# Revit family: QF_EVEREST_ES_3_cat
name_source: partatom
category: Specialty Equipment
revit_build: Autodesk Revit 2015 (Build: 20160512_0715(x64)
units: mm (PartAtom-declared; Revit-internal decimal feet)

## types (2) — shared parameters
Apparent Power = 0 VA
Conn Conduit = Yes
Cycle = 60 Hz
Depth = 803 mm
Foodservice Equipment Identifier = Yes
Height = 2010 mm  [stored 6.59449 ft]
Identify Quantity as Lot = Yes
Length = 1900 mm  [stored 6.2336 ft]
Manufacturer = EVEREST
Max Overcurrent Protection = 0 A
Min Ckt Ampacity = 0 A
Number of Poles = 1
Phase = 1
Refrigerant Volume = 0.00 kip
Volts = 115 V
zero-valued in all types: Elec Conn Connection Height, Elec Conn RI Height

## per-type parameters (varying)
| type | BTUH | Conn Plug | Description | Electrical Remarks | FL Amps | HP | Model | Refrigerant Type | Watts | Weight in Pounds |
| ESF3_115/60/1 | 6870.0 Btu/h | NEMA 5-20P | UPRIGHT REACH–IN FREEZER | HAS (X2) 1/2 HP COMPRESSORS. BTUH IS CALCULATED FOR (2) COMPRESSORS. COMES IN R-404A AND R290 REFRIGERANT VARIANTS. | 12 A | 1/2 (x2) | ESF3 | R-404A / R290 | 1421 W | 661 |
| ESR3_115/60/1 | 4445.0 Btu/h | NEMA 5-15P | UPRIGHT REACH–IN REFRIGERATOR |  | 11 A | 3/4 | ESR3 | R290 | 1279 W | 576 |

note: [stored X ft] marks values corroborated as IEEE doubles in the binary element streams (Revit-internal decimal feet)

## geometry (parser evidence)
native form markers: Sweep x4
no freeform markers — native parametric forms only
